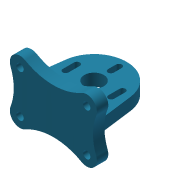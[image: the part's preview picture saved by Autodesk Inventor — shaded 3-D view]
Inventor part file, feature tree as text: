
AUTODESK INVENTOR PART (.ipt)
format: ipt  version: 2014 (Build 180170000, 170)  size: 162,304 bytes
history: native  units: mm
features: extrude x4, sketch x4
ambient origin geometry x8: Origin, YZ Plane, XZ Plane, XY Plane, X Axis, Y Axis, Z Axis, Center Point
bodies: Solid1 (feature_tree)
feature tree (8):
  extrude  "Extrusion1"  Depth=41.0mm
  extrude  "Extrusion2"  Depth=4.0mm
  extrude  "Extrusion3"  Depth=35.0mm
  extrude  "Extrusion4"  Depth=20.0mm
  sketch  "Sketch1"  dims[d0=26.0mm d1=41.0mm]
  sketch  "Sketch2"  dims[d2=4.5mm d3=4.0mm]
  sketch  "Sketch3"  dims[d4=30.0mm d5=35.0mm]
  sketch  "Sketch4"  dims[d6=7.0mm d7=0.0mm d8=20.0mm d9=18.0mm d10=45.0mm d11=7.5mm d12=0.0mm d13=12.0mm d14=7.5mm d15=0.0mm d16=3.6mm d17=5.0mm d18=2.5mm d19=2.5mm d20=14.0mm d21=14.0mm d22=7.0mm d23=7.5mm d24=0.0mm]
